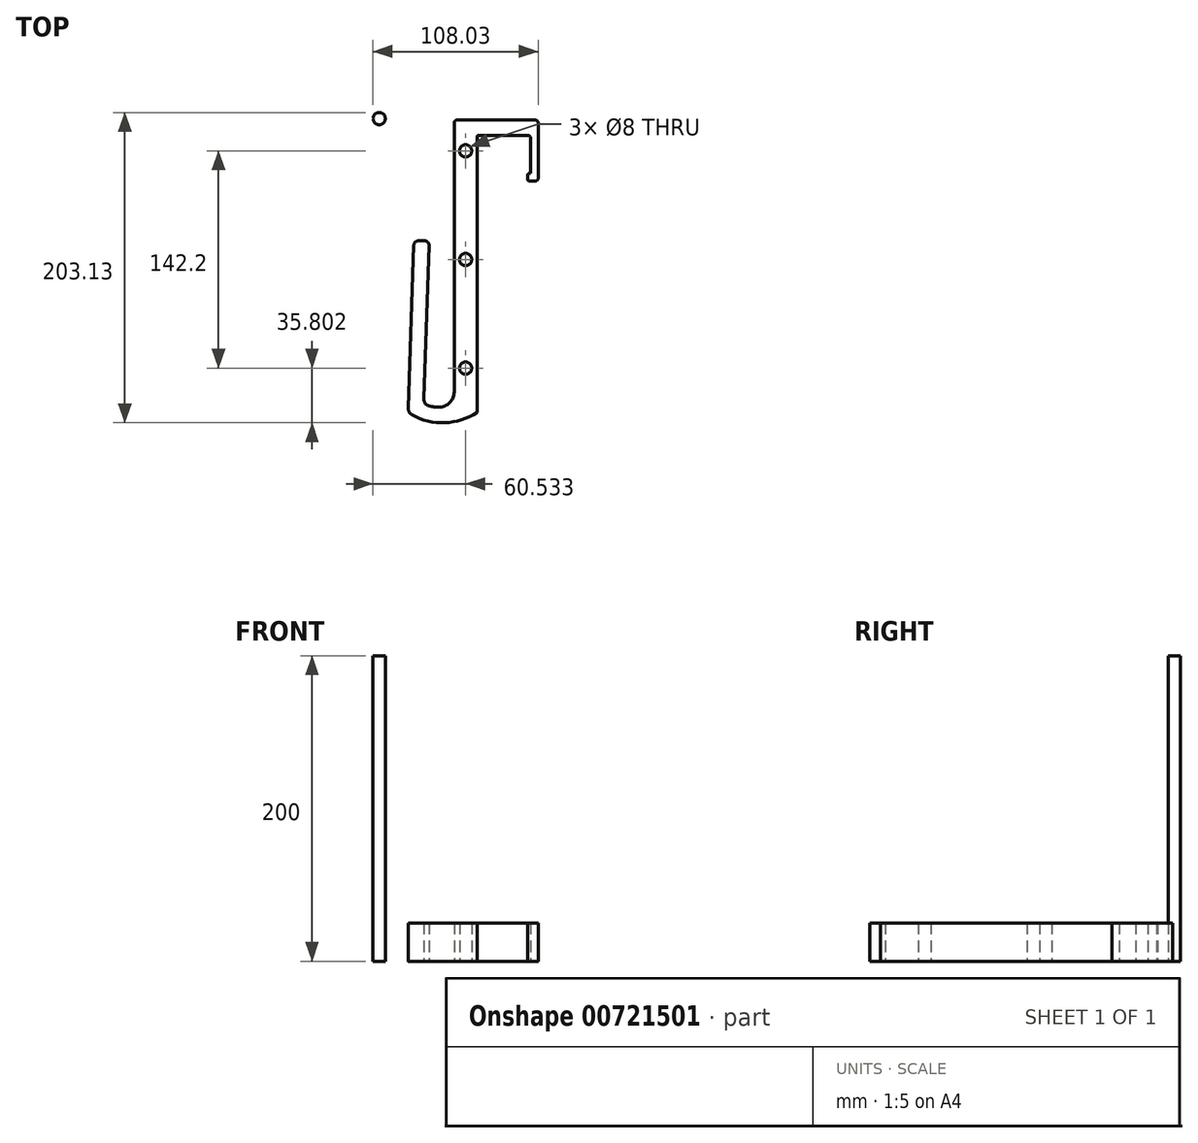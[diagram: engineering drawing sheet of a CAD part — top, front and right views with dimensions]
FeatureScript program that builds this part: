
annotation { "Feature Type Name" : "Feature", "Feature Type Description" : "" }
export const myFeature = defineFeature(function(context is Context, id is Id, definition is map)
    precondition{}
    {
        {
            var Q0;
            Q0=qCreatedBy(makeId("Top.planeOp"),FACE);
            var sketch = newSketch(context, id + "F0", { "sketchPlane" : qUnion([Q0])});
            skLineSegment(sketch, "E0", {"start": v(7.7, 27.7) * mm, "end": v(39.16, 27.7) * mm});
            skLineSegment(sketch, "E1", {"start": v(41.16, 25.7) * mm, "end": v(41.16, 2.7) * mm});
            skLineSegment(sketch, "E2", {"start": v(41.16, -2.3) * mm, "end": v(46.16, -2.3) * mm});
            skLineSegment(sketch, "E3", {"start": v(46.16, -2.3) * mm, "end": v(46.16, 37.7) * mm});
            skLineSegment(sketch, "E4", {"start": v(46.16, 37.7) * mm, "end": v(-8.84, 37.7) * mm});
            skLineSegment(sketch, "E5", {"start": v(-39.02, -153.71) * mm, "end": v(-35.2, -44.27) * mm});
            skLineSegment(sketch, "E6", {"start": v(-32.2, -41.38) * mm, "end": v(-28.2, -41.38) * mm});
            skLineSegment(sketch, "E7", {"start": v(-25.2, -44.48) * mm, "end": v(-28.84, -148.5) * mm});
            skLineSegment(sketch, "E8", {"start": v(-8.84, -140.3) * mm, "end": v(-8.84, 37.7) * mm});
            skPoint(sketch, "E9.visualSharp", {"position": v(43.86, -147.47) * mm});
            skPoint(sketch, "E10.visualSharp", {"position": v(-8.84, -137.3) * mm});
            skPoint(sketch, "E11.visualSharp", {"position": v(-28.63, -142.6) * mm});
            skPoint(sketch, "E12.visualSharp", {"position": v(-25.1, -41.38) * mm});
            skArc(sketch, "E12.filletArc", {"start": v(-25.2, -44.48) * mm, "mid": v(-26.04, -42.3) * mm, "end": v(-28.2, -41.38) * mm});
            skPoint(sketch, "E13.visualSharp", {"position": v(-35.1, -41.38) * mm});
            skArc(sketch, "E13.filletArc", {"start": v(-32.2, -41.38) * mm, "mid": v(-34.28, -42.22) * mm, "end": v(-35.2, -44.27) * mm});
            skPoint(sketch, "E14.visualSharp", {"position": v(-24.3, 27.7) * mm});
            skArc(sketch, "E14.filletArc", {"start": v(7.7, 27.7) * mm, "mid": v(6.85, 27.5) * mm, "end": v(6.16, 26.97) * mm});
            skPoint(sketch, "E15.visualSharp", {"position": v(41.16, 27.7) * mm});
            skArc(sketch, "E15.filletArc", {"start": v(41.16, 25.7) * mm, "mid": v(40.58, 27.12) * mm, "end": v(39.16, 27.7) * mm});
            skLineSegment(sketch, "E16.bottom", {"start": v(41.16, -2.3) * mm, "end": v(40.32, -2.3) * mm});
            skLineSegment(sketch, "E16.top", {"start": v(41.16, 2.7) * mm, "end": v(40.32, 2.7) * mm});
            skLineSegment(sketch, "E16.right", {"start": v(39.32, -1.3) * mm, "end": v(39.32, 1.7) * mm});
            skPoint(sketch, "E17.visualSharp", {"position": v(39.32, 2.7) * mm});
            skArc(sketch, "E17.filletArc", {"start": v(40.32, 2.7) * mm, "mid": v(39.61, 2.4) * mm, "end": v(39.32, 1.7) * mm});
            skPoint(sketch, "E18.visualSharp", {"position": v(39.32, -2.3) * mm});
            skArc(sketch, "E18.filletArc", {"start": v(39.32, -1.3) * mm, "mid": v(39.61, -2) * mm, "end": v(40.32, -2.3) * mm});
            skArc(sketch, "E19", {"start": v(-24.73, -149.68) * mm, "mid": v(-21.8, -150.14) * mm, "end": v(-18.84, -150.3) * mm});
            skLineSegment(sketch, "E20", {"start": v(6.16, 26.97) * mm, "end": v(6.16, -153.71) * mm});
            skArc(sketch, "E21", {"start": v(-39.02, -153.71) * mm, "mid": v(-16.43, -160.51) * mm, "end": v(6.16, -153.71) * mm});
            skLineSegment(sketch, "E22", {"start": v(-28.84, -148.5) * mm, "end": v(-8.84, -148.5) * mm, "construction": true});
            skLineSegment(sketch, "E23", {"start": v(-28.7, -144.61) * mm, "end": v(-21.3, 67.41) * mm, "construction": true});
            skPoint(sketch, "E24.visualSharp", {"position": v(-8.84, -148.5) * mm});
            skArc(sketch, "E24.filletArc", {"start": v(-18.84, -150.3) * mm, "mid": v(-11.77, -147.36) * mm, "end": v(-8.84, -140.3) * mm});
            skPoint(sketch, "E25.visualSharp", {"position": v(-28.84, -148.5) * mm});
            skArc(sketch, "E25.filletArc", {"start": v(-28.7, -144.61) * mm, "mid": v(-27.64, -147.87) * mm, "end": v(-24.73, -149.68) * mm});
            skCircle(sketch, "E26", {"center": v(-1.34, -124.7) * mm, "radius": 4 * mm});
            skLineSegment(sketch, "E27", {"start": v(-8.84, -124.7) * mm, "end": v(6.16, -124.7) * mm, "construction": true});
            skCircle(sketch, "E28.0.1.0", {"center": v(-1.34, -53.6) * mm, "radius": 4 * mm});
            skCircle(sketch, "E28.0.2.0", {"center": v(-1.34, 17.5) * mm, "radius": 4 * mm});
            skLineSegment(sketch, "E28.direction1", {"start": v(-1.34, -124.7) * mm, "end": v(23.66, -124.7) * mm, "construction": true});
            skLineSegment(sketch, "E28.direction2", {"start": v(-1.34, -124.7) * mm, "end": v(-1.34, -53.6) * mm, "construction": true});
            skSolve(sketch);
        }
        {
            var Q0;
            Q0=makeQuery(id+"F0.imprint","IMPRINT",FACE,{"disambiguationData":[TD([[makeQuery(id+"F0.imprint","IMPRINT",EDGE,{"derivedFrom":sQuery(id+"F0.wireOp",EDGE,"E0")}),1.0]])]});
            extrude(context, id + "F1", {"entities" : qUnion([Q0]), "depth" : 25 * mm, "offsetDistance" : 25 * mm});
        }
        {
            var Q0;
            Q0=makeQuery(id+"F1.opExtrude","SWEPT_EDGE",EDGE,{"disambiguationData":[OSD([sQuery(id+"F0.wireOp",EDGE,"E4"),sQuery(id+"F0.wireOp",EDGE,"E8")])]});
            var Q1;
            Q1=makeQuery(id+"F1.opExtrude","SWEPT_EDGE",EDGE,{"disambiguationData":[OSD([sQuery(id+"F0.wireOp",EDGE,"E3"),sQuery(id+"F0.wireOp",EDGE,"E4")])]});
            var Q2;
            Q2=makeQuery(id+"F1.opExtrude","SWEPT_EDGE",EDGE,{"disambiguationData":[OSD([sQuery(id+"F0.wireOp",EDGE,"E2"),sQuery(id+"F0.wireOp",EDGE,"E3")])]});
            fillet(context, id + "F2", {"entities" : qUnion([Q0, Q1, Q2]), "radius" : 2 * mm, "tangentPropagation" : true, "allowEdgeOverflow" : false});
        }
        {
            var Q0;
            Q0=makeQuery(id+"F1.opExtrude","SWEPT_EDGE",EDGE,{"disambiguationData":[OSD([sQuery(id+"F0.wireOp",EDGE,"E5"),sQuery(id+"F0.wireOp",EDGE,"E21")])]});
            fillet(context, id + "F3", {"entities" : qUnion([Q0]), "radius" : 5 * mm, "tangentPropagation" : true, "allowEdgeOverflow" : false});
        }
        {
            var Q0;
            Q0=qCreatedBy(makeId("Top.planeOp"),FACE);
            var sketch = newSketch(context, id + "F4", { "sketchPlane" : qUnion([Q0])});
            skCircle(sketch, "E29", {"center": v(-57.87, 38.62) * mm, "radius": 4 * mm});
            skSolve(sketch);
        }
        {
            var Q0;
            Q0 = qSketchRegion(id + "F4", true);
            extrude(context, id + "F5", {"entities" : qUnion([Q0]), "depth" : 200 * mm, "offsetDistance" : 25 * mm});
        }
    });
